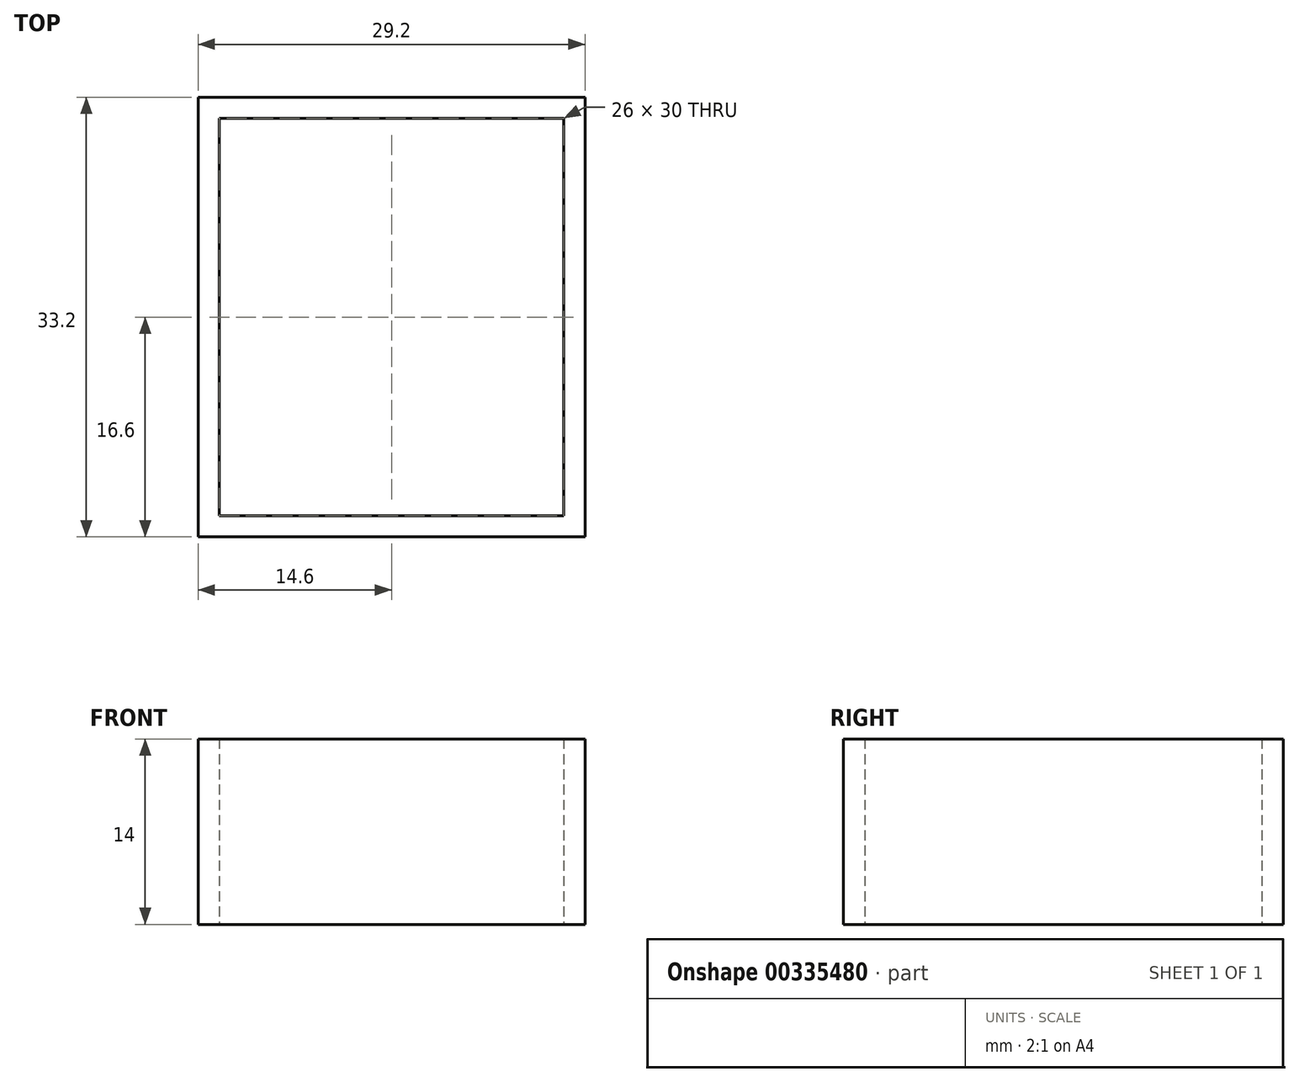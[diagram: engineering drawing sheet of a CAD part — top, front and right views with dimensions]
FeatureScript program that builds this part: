
annotation { "Feature Type Name" : "Feature", "Feature Type Description" : "" }
export const myFeature = defineFeature(function(context is Context, id is Id, definition is map)
    precondition{}
    {
        {
            var Q0;
            Q0=qCreatedBy(makeId("Top.planeOp"),FACE);
            var sketch = newSketch(context, id + "F0", { "sketchPlane" : qUnion([Q0])});
            skLineSegment(sketch, "E0.bottom", {"start": v(-13, 15) * mm, "end": v(13, 15) * mm});
            skLineSegment(sketch, "E0.top", {"start": v(-13, -15) * mm, "end": v(13, -15) * mm});
            skLineSegment(sketch, "E0.left", {"start": v(-13, 15) * mm, "end": v(-13, -15) * mm});
            skLineSegment(sketch, "E0.right", {"start": v(13, 15) * mm, "end": v(13, -15) * mm});
            skLineSegment(sketch, "E1.0", {"start": v(-14.6, 16.6) * mm, "end": v(14.6, 16.6) * mm});
            skLineSegment(sketch, "E1.1", {"start": v(-14.6, 16.6) * mm, "end": v(-14.6, -16.6) * mm});
            skLineSegment(sketch, "E1.2", {"start": v(-14.6, -16.6) * mm, "end": v(14.6, -16.6) * mm});
            skLineSegment(sketch, "E1.3", {"start": v(14.6, 16.6) * mm, "end": v(14.6, -16.6) * mm});
            skSolve(sketch);
        }
        {
            var Q0;
            Q0 = qSketchRegion(id + "F0", true);
            extrude(context, id + "F1", {"entities" : qUnion([Q0]), "depth" : 14 * mm});
        }
    });
